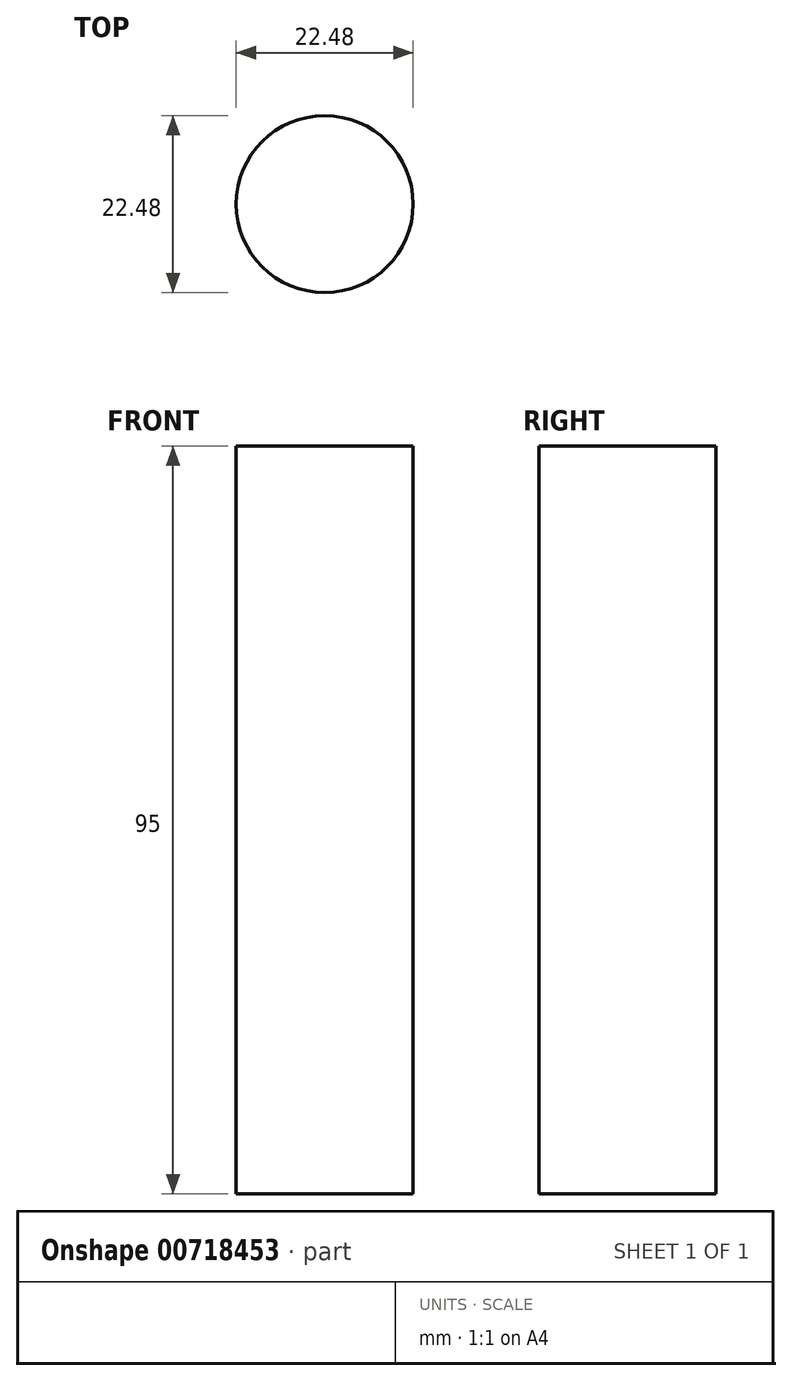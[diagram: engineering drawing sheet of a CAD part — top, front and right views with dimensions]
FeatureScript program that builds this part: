
annotation { "Feature Type Name" : "Feature", "Feature Type Description" : "" }
export const myFeature = defineFeature(function(context is Context, id is Id, definition is map)
    precondition{}
    {
        {
            var Q0;
            Q0=qCreatedBy(makeId("Top.planeOp"),FACE);
            var sketch = newSketch(context, id + "F0", { "sketchPlane" : qUnion([Q0])});
            skCircle(sketch, "E0", {"center": v(0, 0) * mm, "radius": 11.24 * mm});
            skSolve(sketch);
        }
        {
            var Q0;
            Q0=makeQuery(id+"F0.imprint","IMPRINT",FACE,{"disambiguationData":[TD([[makeQuery(id+"F0.imprint","IMPRINT",EDGE,{"derivedFrom":sQuery(id+"F0.wireOp",EDGE,"E0")}),1.0]])]});
            extrude(context, id + "F1", {"entities" : qUnion([Q0]), "depth" : 95 * mm, "offsetDistance" : 25.4 * mm});
        }
        {
            var Q0;
            Q0=qCreatedBy(makeId("Front.planeOp"),FACE);
            var sketch = newSketch(context, id + "F2", { "sketchPlane" : qUnion([Q0])});
            skLineSegment(sketch, "E1", {"start": v(-11.17, 95.07) * mm, "end": v(-13.9, 120.33) * mm});
            skSolve(sketch);
        }
        {
            var Q0;
            Q0=qCreatedBy(makeId("Front.planeOp"),FACE);
            var sketch = newSketch(context, id + "F3", { "sketchPlane" : qUnion([Q0])});
            skLineSegment(sketch, "E2", {"start": v(11.25, 95.12) * mm, "end": v(14.5, 120.31) * mm});
            skSolve(sketch);
        }
        {
            var Q0;
            Q0=makeQuery(id+"F1.opExtrude","CAP_FACE",FACE,{"disambiguationData":[OSD([sQuery(id+"F0.wireOp",EDGE,"E0")])],"isStart":false});
            var Q1;
            Q1=sQuery(id+"F2.wireOp",EDGE,"E1");
            var Q2;
            Q2=sQuery(id+"F3.wireOp",EDGE,"E2");
            var Q3;
            Q3=makeQuery(id+"F1.opExtrude","CAP_EDGE",EDGE,{"disambiguationData":[OSD([sQuery(id+"F0.wireOp",EDGE,"E0")])],"isStart":false});
            revolve(context, id + "F4", {"bodyType" : ToolBodyType.SURFACE, "surfaceOperationType" : NewSurfaceOperationType.NEW, "entities" : qUnion([Q0]), "surfaceEntities" : qUnion([Q1, Q2]), "axis" : qUnion([Q3]), "revolveType" : RevolveType.FULL});
        }
        {
            var Q0;
            Q0=qCreatedBy(makeId("Top.planeOp"),FACE);
            var sketch = newSketch(context, id + "F5", { "sketchPlane" : qUnion([Q0])});
            skCircle(sketch, "E3", {"center": v(0, 0) * mm, "radius": 4.23 * mm});
            skSolve(sketch);
        }
        {
            var Q0;
            Q0=sQuery(id+"F5.wireOp",EDGE,"E3");
            extrude(context, id + "F6", {"bodyType" : ToolBodyType.SURFACE, "surfaceEntities" : qUnion([Q0]), "depth" : 123.82 * mm, "offsetDistance" : 25.4 * mm});
        }
    });
